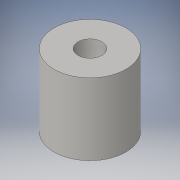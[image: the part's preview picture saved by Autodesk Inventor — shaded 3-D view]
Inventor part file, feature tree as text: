
AUTODESK INVENTOR PART (.ipt)
format: ipt  version: 2016 SP1 (Build 200210100, 210)  size: 99,328 bytes
history: native  units: in
note: dims shown in document units (in); Inventor stores cm internally (conversion verified against a paired STEP export)
features: sketch x3, hole x2, extrude x1
ambient origin geometry x8: Origin, YZ Plane, XZ Plane, XY Plane, X Axis, Y Axis, Z Axis, Center Point
bodies: Solid1 (feature_tree)
feature tree (6):
  extrude  "Extrusion1"  Depth=1.0in TaperAngle=0.0deg
  hole  "Hole1"  [1 undecoded]
  hole  "Hole2"  [1 undecoded]
  sketch  "Sketch1"  dims[d0=1.0in d1=1.0in d2=0.0in]
  sketch  "Sketch2"  dims[d3=0.332in d4=0.75in d5=0.635in d6=0.25in d7=0.5635in d8=0.75in d9=0.8108in]
  sketch  "Sketch3"  dims[d10=0.252in d11=0.5in d12=0.635in d13=0.25in d14=0.5635in d15=0.5in d16=0.8108in]
note: 2 required parameter values undecoded (feature->parameter linkage not recoverable at this tier; creation-order binding heuristic only, values carry confidence <= 0.55)
